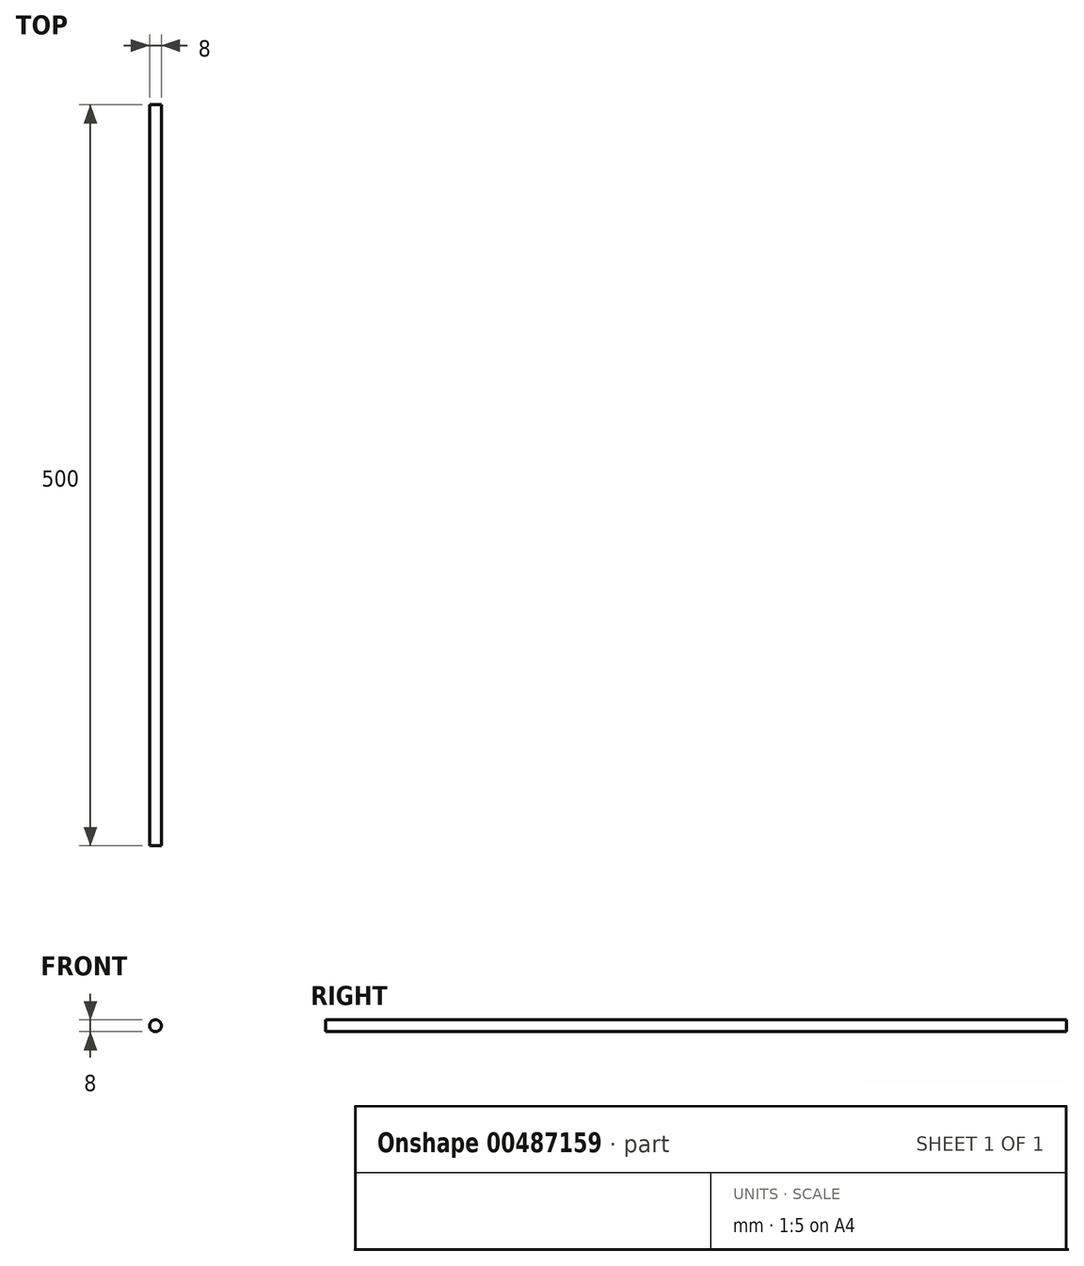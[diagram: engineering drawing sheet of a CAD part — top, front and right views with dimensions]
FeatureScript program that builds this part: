
annotation { "Feature Type Name" : "Feature", "Feature Type Description" : "" }
export const myFeature = defineFeature(function(context is Context, id is Id, definition is map)
    precondition{}
    {
        {
            var Q0;
            Q0=qCreatedBy(makeId("Front.planeOp"),FACE);
            var sketch = newSketch(context, id + "F0", { "sketchPlane" : qUnion([Q0])});
            skCircle(sketch, "E0", {"center": v(0, 0) * mm, "radius": 4 * mm});
            skSolve(sketch);
        }
        {
            var Q0;
            Q0 = qSketchRegion(id + "F0", true);
            extrude(context, id + "F1", {"entities" : qUnion([Q0]), "depth" : 250 * mm, "hasSecondDirection" : true, "secondDirectionOppositeDirection" : true, "secondDirectionDepth" : 250 * mm});
        }
    });
